# Revit family: Haworth_JiveTable_90CornerExtended
name_source: partatom
category: Furniture Systems
revit_build: Autodesk Revit 2018 (Build: 20170223_1515(x64)
units: mm (PartAtom-declared; Revit-internal decimal feet)

## family parameters
Always vertical = Yes
Cut with Voids When Loaded = No
OmniClass Number = 23.40.70.14.64.21
OmniClass Title = Systems Furniture
Part Type = Normal
Room Calculation Point = No
Round Connector Dimension = Use Diameter
Shared = No
Work Plane-Based = No

## types (28) — shared parameters
Actual Height = 29"
Assembly Code = E2020200
Custom Size = No
Leg Finish = Haworth _ Paint _ Graphite
Leg Height = 27 13/16"
Manufacturer = Haworth, Inc.
Max. Depth = 30"
Max. Height = 29"
Max. Length = 72"
Max. Width = 48"
Min. Depth = 18"
Min. Height = 29"
Min. Length = 60"
Min. Width = 42"
Model = Haworth Jive
Revision Number = 0
Size = Verify Final Dim. w/ Haworth
Standard Depths = 18, 24, 30 in.
Standard Length = 60, 72 in.
Standard Widths = 42, 48in.
Table Edge Finish = Haworth _ Laminate _ Putty H-AA
Table Finish = Haworth _ Laminate _ Putty H-AA
Table Thickness = 1 3/16"
URL = http://www.haworth.com
URL - Product = https://www.haworth.com
Warranty = http://haworth.com

## per-type parameters (varying)
| type | Actual Left Depth | Actual Length | Actual Right Depth | Actual Width | Casters | Description | Glides | Left Depth | Length | Right Depth | Width |
| 24/24d 42w 60L - With Casters | 24" | 60" | 24" | 42" | Yes | Haworth Swivel Table Corner Extended Corner Transitional Extended - 24/24d 42w 60L - With Caster | No | 24" | 60" | 24" | 42" |
| 24/24d 42w 72L - With Casters | 24" | 72" | 24" | 42" | Yes | Haworth Swivel Table Corner Extended Corner Transitional Extended - 24/24d 42w 72L - With Caster | No | 24" | 72" | 24" | 42" |
| 24/24d 42w 60L - With Glide | 24" | 60" | 24" | 42" | No | Haworth Swivel Table Corner Extended Corner Transitional Extended - 24/24d 42w 60L - With Glides | Yes | 24" | 60" | 24" | 42" |
| 24/24d 42w 72L - With Glide | 24" | 72" | 24" | 42" | No | Haworth Swivel Table Corner Extended Corner Transitional Extended - 24/24d 42w 72L - With Glides | Yes | 24" | 72" | 24" | 42" |
| 24/24d 48w 60L - With Casters | 24" | 60" | 24" | 48" | Yes | Haworth Swivel Table Corner Extended Corner Transitional Extended - 24/24d 48w 60L - With Caster | No | 24" | 60" | 24" | 48" |
| 24/24d 48w 72L - With Casters | 24" | 72" | 24" | 48" | Yes | Haworth Swivel Table Corner Extended Corner Transitional Extended - 24/24d 48w 72L - With Caster | No | 24" | 72" | 24" | 48" |
| 24/24d 48w 60L - With Glide | 24" | 60" | 24" | 48" | No | Haworth Swivel Table Corner Extended Corner Transitional Extended - 24/24d 48w 60L - With Glides | Yes | 24" | 60" | 24" | 48" |
| 24/24d 48w 72L - With Glide | 24" | 72" | 24" | 48" | No | Haworth Swivel Table Corner Extended Corner Transitional Extended - 24/24d 48w 72L - With Glides | Yes | 24" | 72" | 24" | 48" |
| 30/30d 48w 60L - With Casters | 30" | 60" | 30" | 48" | Yes | Haworth Swivel Table Corner Extended Corner Transitional Extended - 30/30d 48w 60L - With Casters | No | 30" | 60" | 30" | 48" |
| 30/30d 48w 72L - With Casters | 30" | 72" | 30" | 48" | Yes | Haworth Swivel Table Corner Extended Corner Transitional Extended - 30/30d 48w 72L - With Casters | No | 30" | 72" | 30" | 48" |
| 30/30d 48w 60L - With Glide | 30" | 60" | 30" | 48" | No | Haworth Swivel Table Corner Extended Corner Transitional Extended - 30/30d 48w 60L - With Glides | Yes | 30" | 60" | 30" | 48" |
| 30/30d 48w 72L - With Glide | 30" | 72" | 30" | 48" | No | Haworth Swivel Table Corner Extended Corner Transitional Extended - 30/30d 48w 72L - With Glides | Yes | 30" | 72" | 30" | 48" |
| 18/24d 42w 60L - With Casters | 18" | 60" | 24" | 42" | Yes | Haworth Swivel Table Corner Extended Corner Transitional Extended - 18/24d 42w 60L - With Casters | No | 18" | 60" | 24" | 42" |
| 18/24d 42w 72L - With Casters | 18" | 72" | 24" | 42" | Yes | Haworth Swivel Table Corner Extended Corner Transitional Extended - 18/24d 42w 72L - With Casters | No | 18" | 72" | 24" | 42" |
| 18/24d 42w 60L - With Glide | 18" | 60" | 24" | 42" | No | Haworth Swivel Table Corner Extended Corner Transitional Extended - 18/24d 42w 60L - With Glides | Yes | 18" | 60" | 24" | 42" |
| 18/24d 42w 72L - With Glide | 18" | 72" | 24" | 42" | No | Haworth Swivel Table Corner Extended Corner Transitional Extended - 18/24d 42w 72L - With Glides | Yes | 18" | 72" | 24" | 42" |
| 24/18d 42w 60L - With Casters | 24" | 60" | 18" | 42" | Yes | Haworth Swivel Table Corner Extended Corner Transitional Extended - 24/18d 42w 60L - With Casters | No | 24" | 60" | 18" | 42" |
| 24/18d 42w 72L - With Casters | 24" | 72" | 18" | 42" | Yes | Haworth Swivel Table Corner Extended Corner Transitional Extended - 24/18d 42w 72L - With Casters | No | 24" | 72" | 18" | 42" |
| 24/18d 42w 60L - With Glide | 24" | 60" | 18" | 42" | No | Haworth Swivel Table Corner Extended Corner Transitional Extended - 24/18d 42w 60L - With Glides | Yes | 24" | 60" | 18" | 42" |
| 24/18d 42w 72L - With Glide | 24" | 72" | 18" | 42" | No | Haworth Swivel Table Corner Extended Corner Transitional Extended - 24/18d 42w 72L - With Glides | Yes | 24" | 72" | 18" | 42" |
| 24/30d 48w 60L - With Casters | 24" | 60" | 30" | 48" | Yes | Haworth Swivel Table Corner Extended Corner Transitional Extended - 24/30d 48w 60L - With Casters | No | 24" | 60" | 30" | 48" |
| 24/30d 48w 72L - With Casters | 24" | 72" | 30" | 48" | Yes | Haworth Swivel Table Corner Extended Corner Transitional Extended - 24/30d 48w 72L - With Casters | No | 24" | 72" | 30" | 48" |
| 24/30d 48w 60L - With Glide | 24" | 60" | 30" | 48" | No | Haworth Swivel Table Corner Extended Corner Transitional Extended - 24/30d 48w 60L - With Glides | Yes | 24" | 60" | 30" | 48" |
| 24/30d 48w 72L - With Glide | 24" | 72" | 30" | 48" | No | Haworth Swivel Table Corner Extended Corner Transitional Extended - 24/30d 48w 72L - With Glides | Yes | 24" | 72" | 30" | 48" |
| 30/24d 48w 60L - With Casters | 30" | 60" | 24" | 48" | Yes | Haworth Swivel Table Corner Extended Corner Transitional Extended - 30/24d 48w 60L - With Casters | No | 30" | 60" | 24" | 48" |
| 30/24d 48w 72L - With Casters | 30" | 72" | 24" | 48" | Yes | Haworth Swivel Table Corner Extended Corner Transitional Extended - 30/24d 48w 72L - With Casters | No | 30" | 72" | 24" | 48" |
| 30/24d 48w 60L - With Glide | 30" | 60" | 24" | 48" | No | Haworth Swivel Table Corner Extended Corner Transitional Extended - 30/24d 48w 60L - With Glides | Yes | 30" | 60" | 24" | 48" |
| 30/24d 48w 72L - With Glide | 30" | 72" | 24" | 48" | No | Haworth Swivel Table Corner Extended Corner Transitional Extended - 30/24d 48w 72L - With Glides | Yes | 30" | 72" | 24" | 48" |

## geometry (parser evidence)
native form markers: Sweep x5
no freeform markers — native parametric forms only
